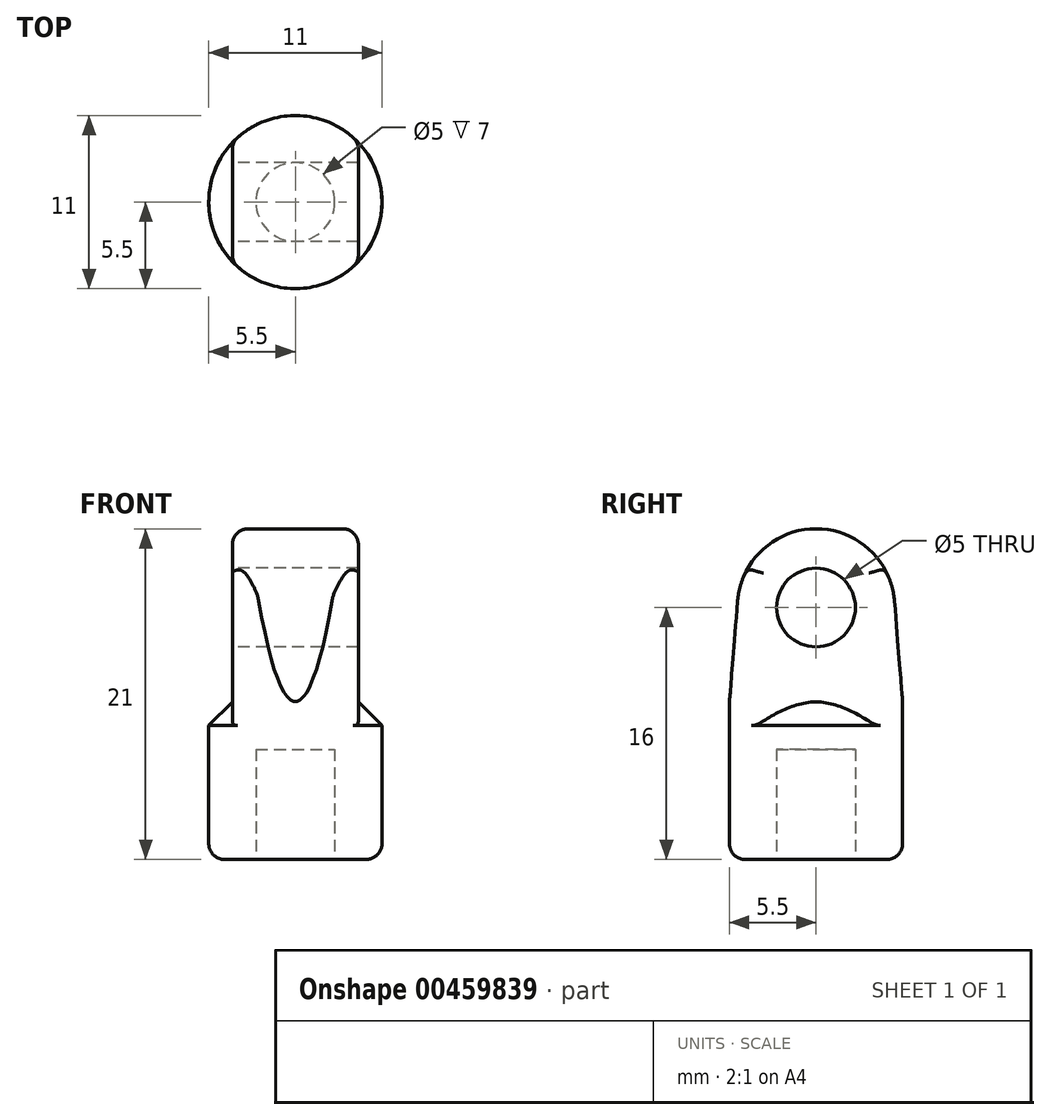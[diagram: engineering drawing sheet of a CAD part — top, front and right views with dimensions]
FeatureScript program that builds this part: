
annotation { "Feature Type Name" : "Feature", "Feature Type Description" : "" }
export const myFeature = defineFeature(function(context is Context, id is Id, definition is map)
    precondition{}
    {
        {
            var Q0;
            Q0=qCreatedBy(makeId("Front.planeOp"),FACE);
            var sketch = newSketch(context, id + "F0", { "sketchPlane" : qUnion([Q0])});
            skLineSegment(sketch, "E0", {"start": v(0, 0) * mm, "end": v(-5.5, 0) * mm});
            skLineSegment(sketch, "E1", {"start": v(-5.5, 0) * mm, "end": v(-5.5, -10) * mm});
            skLineSegment(sketch, "E2", {"start": v(-5.5, -10) * mm, "end": v(-2.5, -10) * mm});
            skLineSegment(sketch, "E3", {"start": v(-2.5, -10) * mm, "end": v(-2.5, -3) * mm});
            skLineSegment(sketch, "E4", {"start": v(-2.5, -3) * mm, "end": v(0, -3) * mm});
            skLineSegment(sketch, "E5", {"start": v(0, -3) * mm, "end": v(0, 0) * mm});
            skSolve(sketch);
        }
        {
            var Q0;
            Q0=qSketchRegion(id+"F0",true);
            var Q1;
            Q1=sQuery(id+"F0.wireOp",EDGE,"E5");
            revolve(context, id + "F1", {"entities" : qUnion([Q0]), "axis" : qUnion([Q1]), "revolveType" : RevolveType.FULL});
        }
        {
            var Q0;
            Q0=qCreatedBy(makeId("Right.planeOp"),FACE);
            var sketch = newSketch(context, id + "F2", { "sketchPlane" : qUnion([Q0])});
            skCircle(sketch, "E6", {"center": v(0, 6) * mm, "radius": 2.5 * mm});
            skCircle(sketch, "E7", {"center": v(0, 6) * mm, "radius": 5 * mm});
            skLineSegment(sketch, "E8", {"start": v(0, 0) * mm, "end": v(-5.5, 0) * mm});
            skLineSegment(sketch, "E9", {"start": v(-5.5, 0) * mm, "end": v(-4.98, 6.4) * mm});
            skLineSegment(sketch, "E10.MirrorCS", {"start": v(5.5, 0) * mm, "end": v(4.98, 6.4) * mm});
            skLineSegment(sketch, "E11", {"start": v(5.5, 0) * mm, "end": v(0, 0) * mm});
            skSolve(sketch);
        }
        {
            var Q0;
            Q0=qSketchRegion(id+"F2",true);
            extrude(context, id + "F3", {"entities" : qUnion([Q0]), "operationType" : NewBodyOperationType.ADD, "endBound" : BoundingType.SYMMETRIC, "depth" : 8 * mm, "offsetDistance" : 25 * mm});
        }
        {
            var Q0;
            Q0=makeQuery(id+"F1.opRevolve","SWEPT_FACE",FACE,{"disambiguationData":[OSD([sQuery(id+"F0.wireOp",EDGE,"E2")])]});
            var sketch = newSketch(context, id + "F4", { "sketchPlane" : qUnion([Q0])});
            skCircle(sketch, "E12", {"center": v(0, 0) * mm, "radius": 5.5 * mm});
            skCircle(sketch, "E13", {"center": v(0, 0) * mm, "radius": 15.5 * mm});
            skSolve(sketch);
        }
        {
            var Q0;
            Q0=qSketchRegion(id+"F4",true);
            extrude(context, id + "F5", {"entities" : qUnion([Q0]), "operationType" : NewBodyOperationType.REMOVE, "endBound" : BoundingType.THROUGH_ALL, "oppositeDirection" : true, "depth" : 25 * mm, "offsetDistance" : 25 * mm});
        }
        {
            var Q0;
            Q0=makeQuery(id+"F3.opExtrude","CAP_EDGE",EDGE,{"disambiguationData":[OSD([sQuery(id+"F2.wireOp",EDGE,"E7")])],"isStart":false});
            var Q1;
            Q1=makeQuery(id+"F3.opExtrude","CAP_EDGE",EDGE,{"disambiguationData":[OSD([sQuery(id+"F2.wireOp",EDGE,"E7")])],"isStart":true});
            var Q2;
            Q2=makeQuery(id+"F1.opRevolve","SWEPT_EDGE",EDGE,{"disambiguationData":[OSD([sQuery(id+"F0.wireOp",EDGE,"E1"),sQuery(id+"F0.wireOp",EDGE,"E2")])]});
            var Q3;
            Q3=makeQuery(id+"F5.boolean.opBoolean","INTERSECT",EDGE,{"disambiguationData":[OD(0.0)],"derivedFrom":[makeQuery(id+"F3.opExtrude","CAP_FACE",FACE,{"disambiguationData":[OSD([sQuery(id+"F2.wireOp",EDGE,"E6"),sQuery(id+"F2.wireOp",EDGE,"E7"),sQuery(id+"F2.wireOp",EDGE,"E8"),sQuery(id+"F2.wireOp",EDGE,"E9"),sQuery(id+"F2.wireOp",EDGE,"E10.MirrorCS"),sQuery(id+"F2.wireOp",EDGE,"E11")])],"isStart":true}),makeQuery(id+"F5.opExtrude","SWEPT_FACE",FACE,{"disambiguationData":[OSD([sQuery(id+"F4.wireOp",EDGE,"E12")])]})]});
            var Q4;
            Q4=makeQuery(id+"F5.boolean.opBoolean","INTERSECT",EDGE,{"disambiguationData":[OD(1.0)],"derivedFrom":[makeQuery(id+"F3.opExtrude","CAP_FACE",FACE,{"disambiguationData":[OSD([sQuery(id+"F2.wireOp",EDGE,"E6"),sQuery(id+"F2.wireOp",EDGE,"E7"),sQuery(id+"F2.wireOp",EDGE,"E8"),sQuery(id+"F2.wireOp",EDGE,"E9"),sQuery(id+"F2.wireOp",EDGE,"E10.MirrorCS"),sQuery(id+"F2.wireOp",EDGE,"E11")])],"isStart":true}),makeQuery(id+"F5.opExtrude","SWEPT_FACE",FACE,{"disambiguationData":[OSD([sQuery(id+"F4.wireOp",EDGE,"E12")])]})]});
            var Q5;
            Q5=makeQuery(id+"F5.boolean.opBoolean","INTERSECT",EDGE,{"disambiguationData":[OD(1.0)],"derivedFrom":[makeQuery(id+"F3.opExtrude","CAP_FACE",FACE,{"disambiguationData":[OSD([sQuery(id+"F2.wireOp",EDGE,"E6"),sQuery(id+"F2.wireOp",EDGE,"E7"),sQuery(id+"F2.wireOp",EDGE,"E8"),sQuery(id+"F2.wireOp",EDGE,"E9"),sQuery(id+"F2.wireOp",EDGE,"E10.MirrorCS"),sQuery(id+"F2.wireOp",EDGE,"E11")])],"isStart":false}),makeQuery(id+"F5.opExtrude","SWEPT_FACE",FACE,{"disambiguationData":[OSD([sQuery(id+"F4.wireOp",EDGE,"E12")])]})]});
            var Q6;
            Q6=makeQuery(id+"F5.boolean.opBoolean","INTERSECT",EDGE,{"disambiguationData":[OD(0.0)],"derivedFrom":[makeQuery(id+"F3.opExtrude","CAP_FACE",FACE,{"disambiguationData":[OSD([sQuery(id+"F2.wireOp",EDGE,"E6"),sQuery(id+"F2.wireOp",EDGE,"E7"),sQuery(id+"F2.wireOp",EDGE,"E8"),sQuery(id+"F2.wireOp",EDGE,"E9"),sQuery(id+"F2.wireOp",EDGE,"E10.MirrorCS"),sQuery(id+"F2.wireOp",EDGE,"E11")])],"isStart":false}),makeQuery(id+"F5.opExtrude","SWEPT_FACE",FACE,{"disambiguationData":[OSD([sQuery(id+"F4.wireOp",EDGE,"E12")])]})]});
            fillet(context, id + "F6", {"entities" : qUnion([Q0, Q1, Q2, Q3, Q4, Q5, Q6]), "radius" : 1 * mm, "tangentPropagation" : true, "allowEdgeOverflow" : false});
        }
        {
            var Q0;
            {var subQ0=sQuery(id+"F0.wireOp",EDGE,"E0");var subQ1=makeQuery(id+"F1.opRevolve","SWEPT_FACE",FACE,{"disambiguationData":[OSD([subQ0])]});var subQ2=sQuery(id+"F2.wireOp",EDGE,"E11");var subQ3=sQuery(id+"F2.wireOp",EDGE,"E8");var subQ4=sQuery(id+"F0.wireOp",EDGE,"E1");var subQ5=makeQuery(id+"F1.opRevolve","SWEPT_FACE",FACE,{"disambiguationData":[OSD([subQ4])]});Q0=makeQuery(id+"F3.boolean.opBoolean","SPLIT",EDGE,{"disambiguationData":[topologyDisambiguationEdgeConnected([subQ1,subQ5]),TD([makeQuery(id+"F3.opExtrude","CAP_FACE",FACE,{"disambiguationData":[OSD([sQuery(id+"F2.wireOp",EDGE,"E6"),sQuery(id+"F2.wireOp",EDGE,"E7"),subQ3,sQuery(id+"F2.wireOp",EDGE,"E9"),sQuery(id+"F2.wireOp",EDGE,"E10.MirrorCS"),subQ2])],"isStart":false})])],"derivedFrom":makeQuery(id+"F1.opRevolve","SWEPT_EDGE",EDGE,{"disambiguationData":[OSD([subQ0,subQ4])]})});}
            var Q1;
            {var subQ0=sQuery(id+"F0.wireOp",EDGE,"E0");var subQ1=makeQuery(id+"F1.opRevolve","SWEPT_FACE",FACE,{"disambiguationData":[OSD([subQ0])]});var subQ2=sQuery(id+"F0.wireOp",EDGE,"E1");var subQ3=makeQuery(id+"F1.opRevolve","SWEPT_FACE",FACE,{"disambiguationData":[OSD([subQ2])]});var subQ4=sQuery(id+"F2.wireOp",EDGE,"E11");var subQ5=sQuery(id+"F2.wireOp",EDGE,"E8");Q1=makeQuery(id+"F3.boolean.opBoolean","SPLIT",EDGE,{"disambiguationData":[topologyDisambiguationEdgeConnected([subQ1,subQ3]),TD([makeQuery(id+"F3.opExtrude","CAP_FACE",FACE,{"disambiguationData":[OSD([sQuery(id+"F2.wireOp",EDGE,"E6"),sQuery(id+"F2.wireOp",EDGE,"E7"),subQ5,sQuery(id+"F2.wireOp",EDGE,"E9"),sQuery(id+"F2.wireOp",EDGE,"E10.MirrorCS"),subQ4])],"isStart":true})])],"derivedFrom":makeQuery(id+"F1.opRevolve","SWEPT_EDGE",EDGE,{"disambiguationData":[OSD([subQ0,subQ2])]})});}
            chamfer(context, id + "F7", {"entities" : qUnion([Q0, Q1]), "width" : 1.5 * mm, "tangentPropagation" : true});
        }
    });
